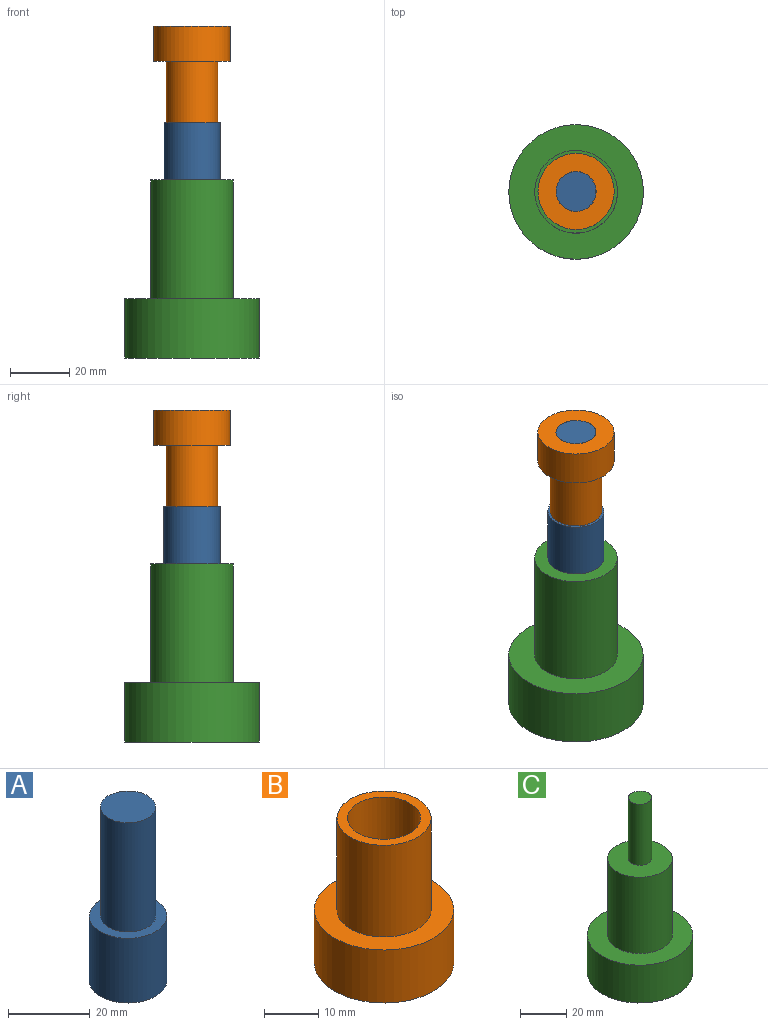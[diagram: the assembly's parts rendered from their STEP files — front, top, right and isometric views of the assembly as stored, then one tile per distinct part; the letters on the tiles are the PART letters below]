
ASSEMBLY  parts=3 mates=4
PART A: 7 faces, bbox 19x19x52.2 mm
  f0: cylinder r=9.5mm len=19.4mm, axis (0,0,-1), area 1158mm2, adj f1,f2
  f1: plane 19x19mm, normal (0,0,1), area 140.4mm2, adj f0,f3
  f2: plane 19x19mm, normal (0,0,-1), area 204.2mm2, adj f0,f5
  f3: cylinder r=6.75mm len=32.76mm, axis (0,0,-1), area 1389.4mm2, adj f1,f4
  f4: plane 13.5x13.5mm, normal (0,0,1), area 143.1mm2, adj f3
  f5: cylinder r=5.03mm len=33mm, axis (0,0,-1), area 1041.9mm2, adj f2,f6
  f6: plane 10.05x10.05mm, normal (0,0,-1), area 79.3mm2, adj f5
PART B: 6 faces, bbox 25.8x25.8x32.8 mm
  f0: cylinder r=12.9mm len=25.8mm, axis (0,0,-1), area 972.6mm2, adj f1,f2
  f1: plane 25.8x25.8mm, normal (0,0,1), area 284.5mm2, adj f0,f3
  f2: plane 25.8x25.8mm, normal (0,0,-1), area 378.6mm2, adj f0,f5
  f3: cylinder r=8.71mm len=20.76mm, axis (0,0,-1), area 1136.1mm2, adj f1,f4
  f4: plane 17.42x17.42mm, normal (0,0,1), area 94.1mm2, adj f3,f5
  f5: cylinder r=6.77mm len=32.76mm, axis (0,0,1), area 1394.5mm2, adj f2,f4
PART C: 7 faces, bbox 45.5x45.5x92.5 mm
  f0: cylinder r=14mm len=40.3mm, axis (0,0,-1), area 3545mm2, adj f1,f4
  f1: plane 28x28mm, normal (0,0,1), area 537.2mm2, adj f0,f5
  f2: cylinder r=22.77mm len=45.55mm, axis (0,0,1), area 2861.7mm2, adj f3,f4
  f3: plane 45.55x45.55mm, normal (0,0,-1), area 1629.2mm2, adj f2
  f4: plane 45.55x45.55mm, normal (0,0,1), area 1013.5mm2, adj f0,f2
  f5: cylinder r=5mm len=32.24mm, axis (0,0,-1), area 1012.8mm2, adj f1,f6
  f6: plane 10x10mm, normal (0,0,1), area 78.5mm2, adj f5
PLACE A t=(0,0,69.3)mm
PLACE B rot(axis=(0,1,0),180deg) t=(0,0,121.46)mm
PLACE C t=(0,0,29)mm
MATE slider A.f0 <-> C.f5  axis (0,0,-1) through (0,0,69.3)mm
MATE planar A.f0 <-> C.f0  axis (0,0,-1) through (0,0,69.3)mm
MATE slider C.f5 <-> B.f3  axis (0,0,-1) through (0,0,85.42)mm
MATE planar B.f0 <-> A.f0  axis (0,0,-1) through (0,0,88.7)mm
